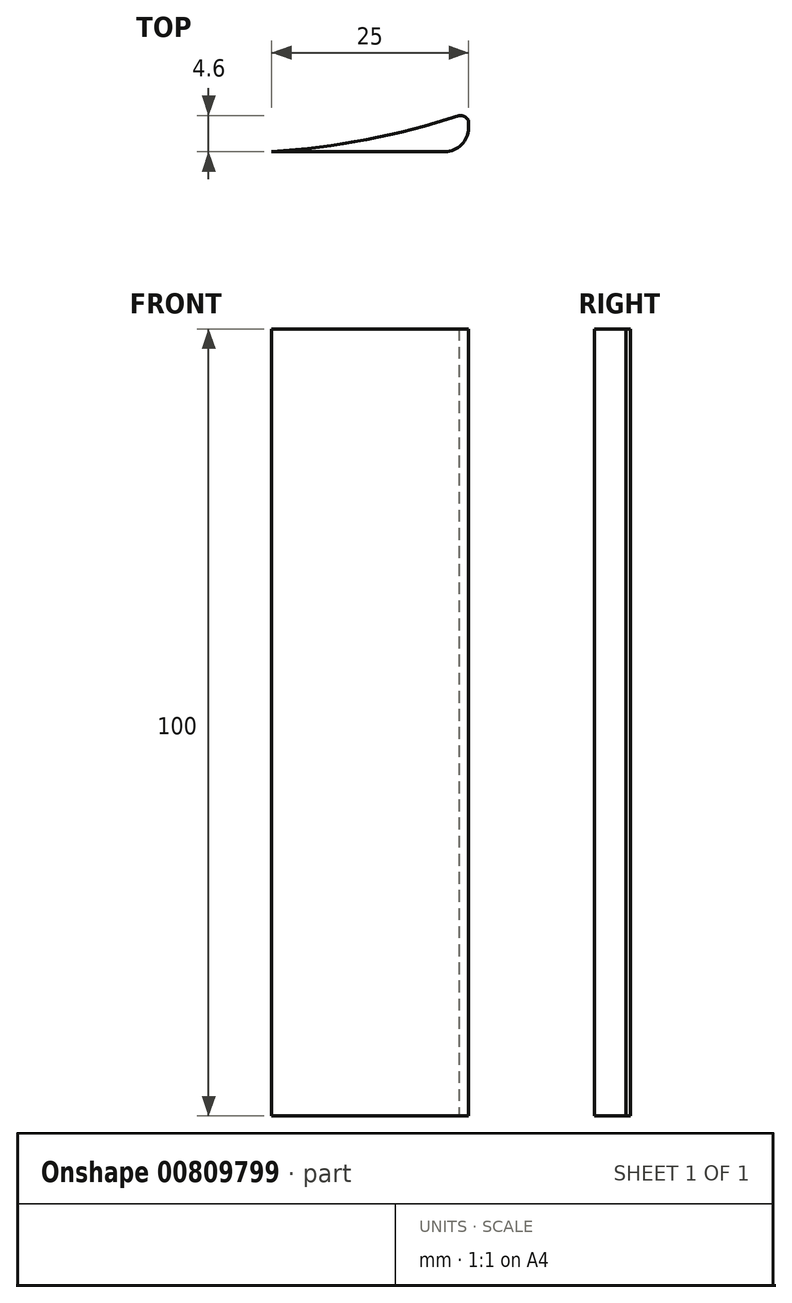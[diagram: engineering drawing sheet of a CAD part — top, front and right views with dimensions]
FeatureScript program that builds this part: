
annotation { "Feature Type Name" : "Feature", "Feature Type Description" : "" }
export const myFeature = defineFeature(function(context is Context, id is Id, definition is map)
    precondition{}
    {
        {
            var Q0;
            Q0=qCreatedBy(makeId("Top.planeOp"),FACE);
            var sketch = newSketch(context, id + "F0", { "sketchPlane" : qUnion([Q0])});
            skLineSegment(sketch, "E0", {"start": v(-3, 0) * mm, "end": v(-25, 0) * mm});
            skLineSegment(sketch, "E1", {"start": v(0, 4) * mm, "end": v(0, 3) * mm});
            skArc(sketch, "E2", {"start": v(-25, 0) * mm, "mid": v(-12.97, 1.54) * mm, "end": v(-1.22, 4.59) * mm});
            skPoint(sketch, "E3.visualSharp", {"position": v(0, 0) * mm});
            skArc(sketch, "E3.filletArc", {"start": v(-3, 0) * mm, "mid": v(-0.88, 0.88) * mm, "end": v(0, 3) * mm});
            skArc(sketch, "E4", {"start": v(0, 4) * mm, "mid": v(-0.72, 4.56) * mm, "end": v(-1.63, 4.46) * mm});
            skPoint(sketch, "E5.orphan", {"position": v(0, 5) * mm});
            skSolve(sketch);
        }
        {
            var Q0;
            {var subQ4=sQuery(id+"F0.wireOp",EDGE,"E0");Q0=makeQuery(id+"F0.imprint","IMPRINT",FACE,{"disambiguationData":[TD([[makeQuery(id+"F0.imprint","IMPRINT",EDGE,{"derivedFrom":subQ4}),-1.0]])]});}
            extrude(context, id + "F1", {"entities" : qUnion([Q0]), "depth" : 100 * mm, "offsetDistance" : 25 * mm});
        }
    });
